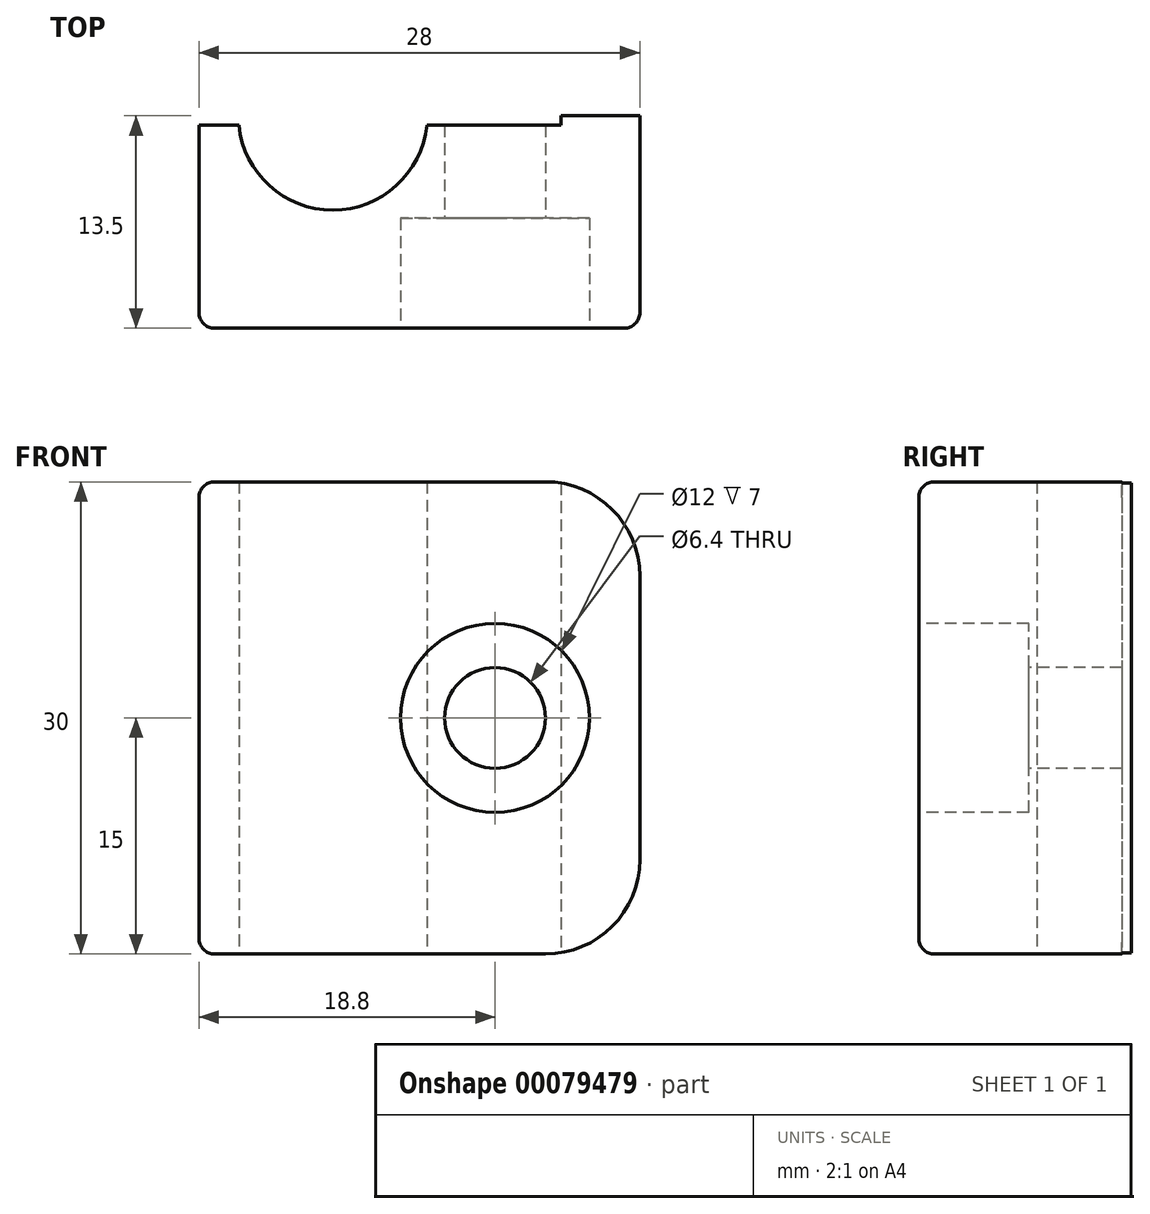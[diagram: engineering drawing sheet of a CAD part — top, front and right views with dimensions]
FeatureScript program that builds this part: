
annotation { "Feature Type Name" : "Feature", "Feature Type Description" : "" }
export const myFeature = defineFeature(function(context is Context, id is Id, definition is map)
    precondition{}
    {
        {
            var Q0;
            Q0=qCreatedBy(makeId("Top.planeOp"),FACE);
            var sketch = newSketch(context, id + "F0", { "sketchPlane" : qUnion([Q0])});
            skLineSegment(sketch, "E0.bottom", {"start": v(-14, 0) * mm, "end": v(14, 0) * mm});
            skLineSegment(sketch, "E0.top", {"start": v(-14, -13.5) * mm, "end": v(14, -13.5) * mm});
            skLineSegment(sketch, "E0.left", {"start": v(-14, 0) * mm, "end": v(-14, -13.5) * mm});
            skLineSegment(sketch, "E0.right", {"start": v(14, 0) * mm, "end": v(14, -13.5) * mm});
            skLineSegment(sketch, "E1", {"start": v(-14, -0.6) * mm, "end": v(9, -0.6) * mm});
            skLineSegment(sketch, "E2", {"start": v(9, -0.6) * mm, "end": v(9, 0) * mm});
            skCircle(sketch, "E3", {"center": v(-5.5, 0) * mm, "radius": 6 * mm});
            skPoint(sketch, "E4.visualSharp", {"position": v(-14, -13.5) * mm});
            skPoint(sketch, "E5.visualSharp", {"position": v(14, -13.5) * mm});
            skSolve(sketch);
        }
        {
            var Q0;
            Q0=makeQuery(id+"F0.imprint","IMPRINT",FACE,{"disambiguationData":[TD([[makeQuery(id+"F0.imprint","IMPRINT",EDGE,{"derivedFrom":sQuery(id+"F0.wireOp",EDGE,"E0.top")}),1.0]])]});
            extrude(context, id + "F1", {"entities" : qUnion([Q0]), "depth" : 30 * mm, "offsetDistance" : 25 * mm});
        }
        {
            var Q0;
            Q0=makeQuery(id+"F1.opExtrude","SWEPT_FACE",FACE,{"disambiguationData":[OSD([sQuery(id+"F0.wireOp",EDGE,"E0.top")])]});
            var sketch = newSketch(context, id + "F2", { "sketchPlane" : qUnion([Q0])});
            skCircle(sketch, "E6", {"center": v(4.8, 15) * mm, "radius": 6 * mm});
            skLineSegment(sketch, "E7", {"start": v(40.23, 15) * mm, "end": v(-30.63, 15) * mm, "construction": true});
            skCircle(sketch, "E8", {"center": v(4.8, 15) * mm, "radius": 3.2 * mm});
            skSolve(sketch);
        }
        {
            var Q0;
            Q0 = qSketchRegion(id + "F2", true);
            extrude(context, id + "F3", {"entities" : qUnion([Q0]), "operationType" : NewBodyOperationType.REMOVE, "oppositeDirection" : true, "depth" : 7 * mm, "offsetDistance" : 25 * mm});
        }
        {
            var Q0;
            Q0=makeQuery(id+"F3.boolean.opBoolean","SPLIT",FACE,{"disambiguationData":[TD([makeQuery(id+"F3.opExtrude","SWEPT_FACE",FACE,{"disambiguationData":[OSD([sQuery(id+"F2.wireOp",EDGE,"E8")])]})])],"derivedFrom":makeQuery(id+"F1.opExtrude","SWEPT_FACE",FACE,{"disambiguationData":[OSD([sQuery(id+"F0.wireOp",EDGE,"E0.top")])]})});
            extrude(context, id + "F4", {"entities" : qUnion([Q0]), "operationType" : NewBodyOperationType.REMOVE, "oppositeDirection" : true, "depth" : 25 * mm, "offsetDistance" : 25 * mm});
        }
        {
            var Q0;
            Q0=makeQuery(id+"F1.opExtrude","CAP_EDGE",EDGE,{"disambiguationData":[OSD([sQuery(id+"F0.wireOp",EDGE,"E0.right")])],"isStart":true});
            var Q1;
            Q1=makeQuery(id+"F1.opExtrude","CAP_EDGE",EDGE,{"disambiguationData":[OSD([sQuery(id+"F0.wireOp",EDGE,"E0.right")])],"isStart":false});
            fillet(context, id + "F5", {"entities" : qUnion([Q0, Q1]), "radius" : 6 * mm, "tangentPropagation" : true, "allowEdgeOverflow" : false});
        }
        {
            var Q0;
            Q0=makeQuery(id+"F1.opExtrude","CAP_EDGE",EDGE,{"disambiguationData":[OSD([sQuery(id+"F0.wireOp",EDGE,"E0.top")])],"isStart":false});
            var Q1;
            Q1=makeQuery(id+"F1.opExtrude","SWEPT_EDGE",EDGE,{"disambiguationData":[OSD([sQuery(id+"F0.wireOp",EDGE,"E0.top"),sQuery(id+"F0.wireOp",EDGE,"E0.left")])]});
            var Q2;
            Q2=makeQuery(id+"F1.opExtrude","CAP_EDGE",EDGE,{"disambiguationData":[OSD([sQuery(id+"F0.wireOp",EDGE,"E0.left")])],"isStart":false});
            var Q3;
            Q3=makeQuery(id+"F1.opExtrude","CAP_EDGE",EDGE,{"disambiguationData":[OSD([sQuery(id+"F0.wireOp",EDGE,"E0.left")])],"isStart":true});
            var Q4;
            Q4=makeQuery(id+"F3.boolean.opBoolean","COPY",EDGE,{"derivedFrom":makeQuery(id+"F3.opExtrude","CAP_EDGE",EDGE,{"disambiguationData":[OSD([sQuery(id+"F2.wireOp",EDGE,"E6")])],"isStart":true})});
            fillet(context, id + "F6", {"entities" : qUnion([Q0, Q1, Q2, Q3, Q4]), "radius" : 1 * mm, "tangentPropagation" : true, "allowEdgeOverflow" : false});
        }
    });
